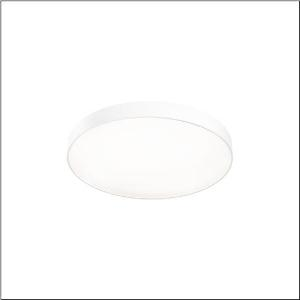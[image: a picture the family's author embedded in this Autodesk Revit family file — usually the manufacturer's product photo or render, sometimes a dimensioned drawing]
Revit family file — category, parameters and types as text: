
# Revit family: round_21_m_51mr36fm8421w
name_source: partatom
category: Lighting Fixtures
units: mm (PartAtom-declared; Revit-internal decimal feet)

## family parameters
Cut with Voids When Loaded = No
Host = Face
Light Source = No
Part Type = Normal
Room Calculation Point = No
Round Connector Dimension = Use Diameter
Shared = No

## types (1)
- --- (1 x LED, 8900 lm, 62.6 W, 4000K)
    Apparent Load = 63 VA
    CIE Flux Codes = 49 80 96 100 100
    Color Rendering = 80
    Color Temperature = 4000K
    Default Elevation = 1800 mm
    Description = Round 21 M, wall and ceiling luminaire, primary optical cover: cover, of PMMA, opal, light emission: direct distribution, primary light characteristic: symmetric, installation type: surface-mounted, suspended mounting, LED, rated luminous flux: 8.140lm, luminous efficacy: 133lm/W, light colour: 840, colour temperature: 4000K, control gear: ON/OFF Multilumen, with terminal, 3-pole, mains connection: 230V, AC, 50/60Hz, rated input power: 61W, housing, of aluminium, coated, white, diameter: 600mm, height: 62mm, protection rating (complete): IP40, insulation class (complete): insulation class I (protective earthing), certification: CE, impact resistance: IK04, permissible operating ambient temperature: -10..+35°C, packaging unit: 1 piece
    Height = 87 mm
    Lamp = 1 x LED
    Lamp Light Flux = 8900 lm
    Lamp Power = 62.6 W
    Lamp count = 1
    Length = 600 mm
    Luminous efficacy = 142 lm/W
    Manufacturer = Siteco
    ModVariant = No
    Model = 51MR36FM8421W
    Mounting Place = Ceiling
    Mounting Type = Surface mounted
    Number of Poles = 1
    OnlyDefault = Yes
    Power Factor = 1
    Product Name = Round 21 M
    Product group = wall and ceiling luminaire | ceiling mounted
    ProductGroupID = 304
    Protection Class = Protection class I
    Protection Degree = IP 40
    RLX_Detail_Level = 1
    RLX_Emergency_Light_Flux = 0 lm
    RLX_Emergency_Type = 0
    RLX_Emergency_Type_DB = No
    RlxData = <blob elided: 14393 chars, md5=69b354b6>
    Socket = socket
    Standby Power = 0 W
    System Light Flux = 8900 lm
    System Power = 63 W
    Type Comments = factory setting: luminous flux: 100 % | (ON | ON | ON | ON) | 700 mA
    Type Image = l_1258330.jpg
    URL = http://relux.com
    VarID = @adj_041107
    Voltage = 0 V
    Weight = 0.00 kg
    Width = 0 mm  [stored 0 ft]

note: [stored X ft] marks values corroborated as IEEE doubles in the binary element streams (Revit-internal decimal feet)

## geometry (parser evidence)
native form markers: Sweep x13
no freeform markers — native parametric forms only
